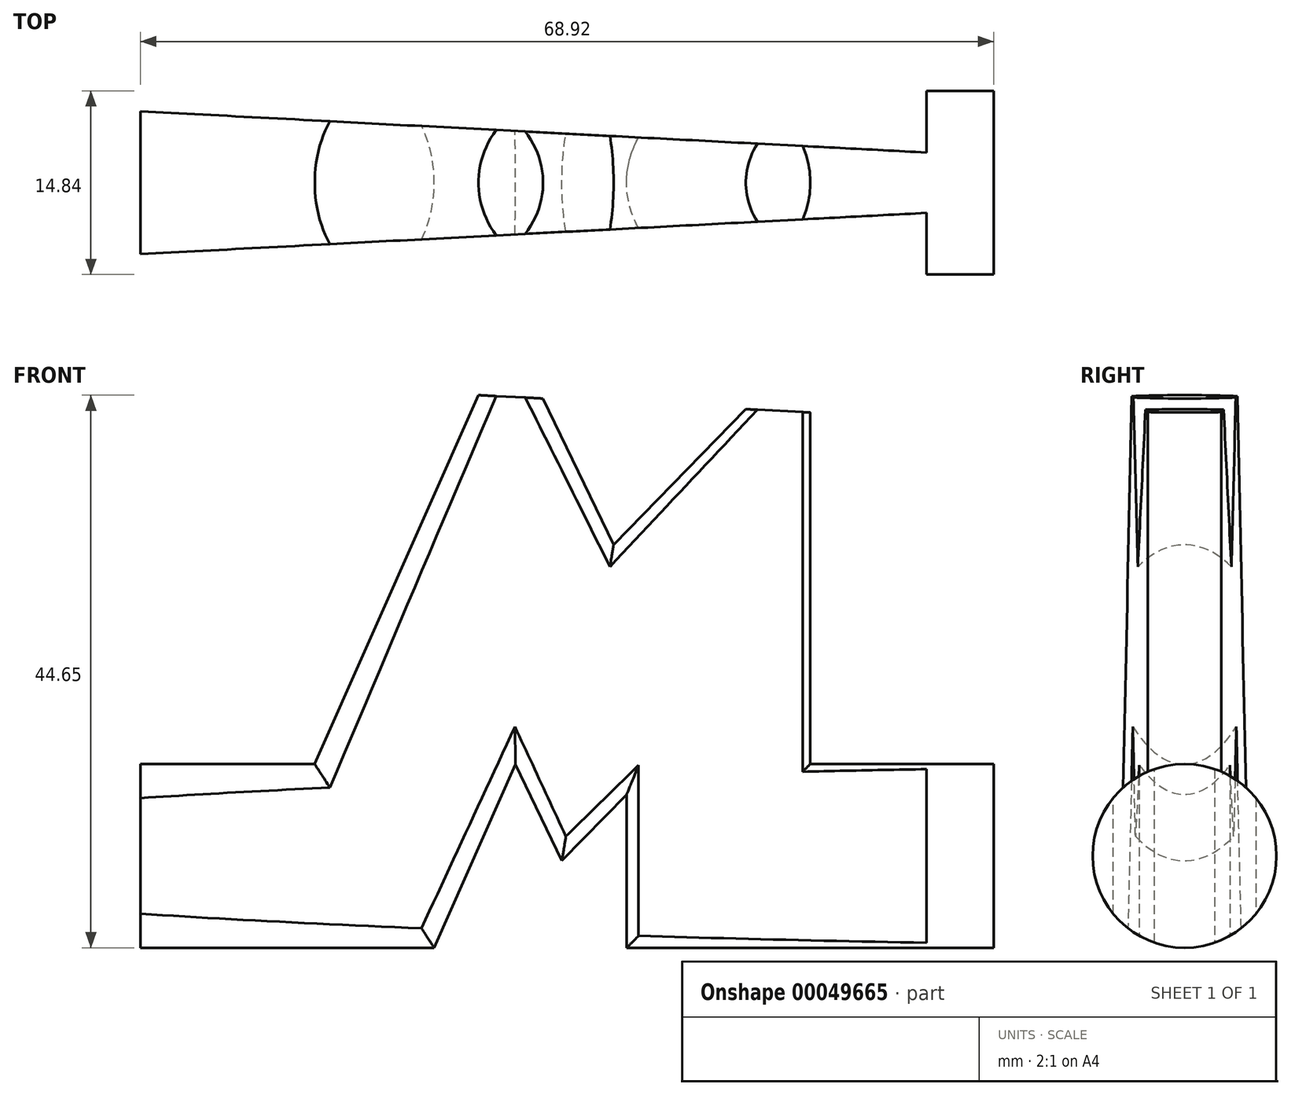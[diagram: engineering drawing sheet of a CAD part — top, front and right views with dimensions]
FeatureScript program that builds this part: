
annotation { "Feature Type Name" : "Feature", "Feature Type Description" : "" }
export const myFeature = defineFeature(function(context is Context, id is Id, definition is map)
    precondition{}
    {
        {
            var Q0;
            Q0=qCreatedBy(makeId("Front.planeOp"),FACE);
            var sketch = newSketch(context, id + "F0", { "sketchPlane" : qUnion([Q0])});
            skLineSegment(sketch, "E0", {"start": v(0, 0) * mm, "end": v(18.9, 0) * mm});
            skLineSegment(sketch, "E1", {"start": v(18.9, 0) * mm, "end": v(30.01, 25.06) * mm});
            skLineSegment(sketch, "E2", {"start": v(30.01, 25.06) * mm, "end": v(36.13, 12.37) * mm});
            skLineSegment(sketch, "E3", {"start": v(36.13, 12.37) * mm, "end": v(46.69, 23.2) * mm});
            skLineSegment(sketch, "E4", {"start": v(46.69, 23.2) * mm, "end": v(46.69, 0) * mm});
            skLineSegment(sketch, "E5", {"start": v(46.69, 0) * mm, "end": v(68.92, 0) * mm});
            skSolve(sketch);
        }
        {
            var Q0;
            Q0=qCreatedBy(makeId("Right.planeOp"),FACE);
            var sketch = newSketch(context, id + "F1", { "sketchPlane" : qUnion([Q0])});
            skCircle(sketch, "E6", {"center": v(0, 0) * mm, "radius": 7.42 * mm});
            skSolve(sketch);
        }
        {
            var Q0;
            Q0=makeQuery(id+"F1.imprint","IMPRINT",FACE,{"disambiguationData":[TD([[makeQuery(id+"F1.imprint","IMPRINT",EDGE,{"derivedFrom":sQuery(id+"F1.wireOp",EDGE,"E6")}),1.0]])]});
            var Q1;
            Q1=sQuery(id+"F0.wireOp",EDGE,"E0");
            var Q2;
            Q2=sQuery(id+"F0.wireOp",EDGE,"E1");
            var Q3;
            Q3=sQuery(id+"F0.wireOp",EDGE,"E2");
            var Q4;
            Q4=sQuery(id+"F0.wireOp",EDGE,"E3");
            var Q5;
            Q5=sQuery(id+"F0.wireOp",EDGE,"E4");
            var Q6;
            Q6=sQuery(id+"F0.wireOp",EDGE,"E5");
            sweep(context, id + "F2", {"profiles" : qUnion([Q0]), "path" : qUnion([Q1, Q2, Q3, Q4, Q5, Q6])});
        }
        {
            var Q0;
            Q0=qCreatedBy(makeId("Right.planeOp"),FACE);
            var sketch = newSketch(context, id + "F3", { "sketchPlane" : qUnion([Q0])});
            skLineSegment(sketch, "E7.rect.bottom", {"start": v(5.77, 38.66) * mm, "end": v(-5.77, 38.66) * mm});
            skLineSegment(sketch, "E7.rect.top", {"start": v(5.77, -38.66) * mm, "end": v(-5.77, -38.66) * mm});
            skLineSegment(sketch, "E7.rect.left", {"start": v(5.77, 38.66) * mm, "end": v(5.77, -38.66) * mm});
            skLineSegment(sketch, "E7.rect.right", {"start": v(-5.77, 38.66) * mm, "end": v(-5.77, -38.66) * mm});
            skPoint(sketch, "E7.rect.middle", {"position": v(0, 0) * mm});
            skLineSegment(sketch, "E8.0", {"start": v(12.12, 45.01) * mm, "end": v(12.12, -45.01) * mm});
            skLineSegment(sketch, "E8.1", {"start": v(12.12, 45.01) * mm, "end": v(-12.12, 45.01) * mm});
            skLineSegment(sketch, "E8.2", {"start": v(-12.12, 45.01) * mm, "end": v(-12.12, -45.01) * mm});
            skLineSegment(sketch, "E8.3", {"start": v(12.12, -45.01) * mm, "end": v(-12.12, -45.01) * mm});
            skSolve(sketch);
        }
        {
            var Q0;
            Q0 = qSketchRegion(id + "F3", true);
            extrude(context, id + "F4", {"entities" : qUnion([Q0]), "operationType" : NewBodyOperationType.REMOVE, "endBound" : BoundingType.SYMMETRIC, "oppositeDirection" : true, "depth" : 127 * mm, "hasDraft" : true, "draftAngle" : 3 * degree});
        }
    });
